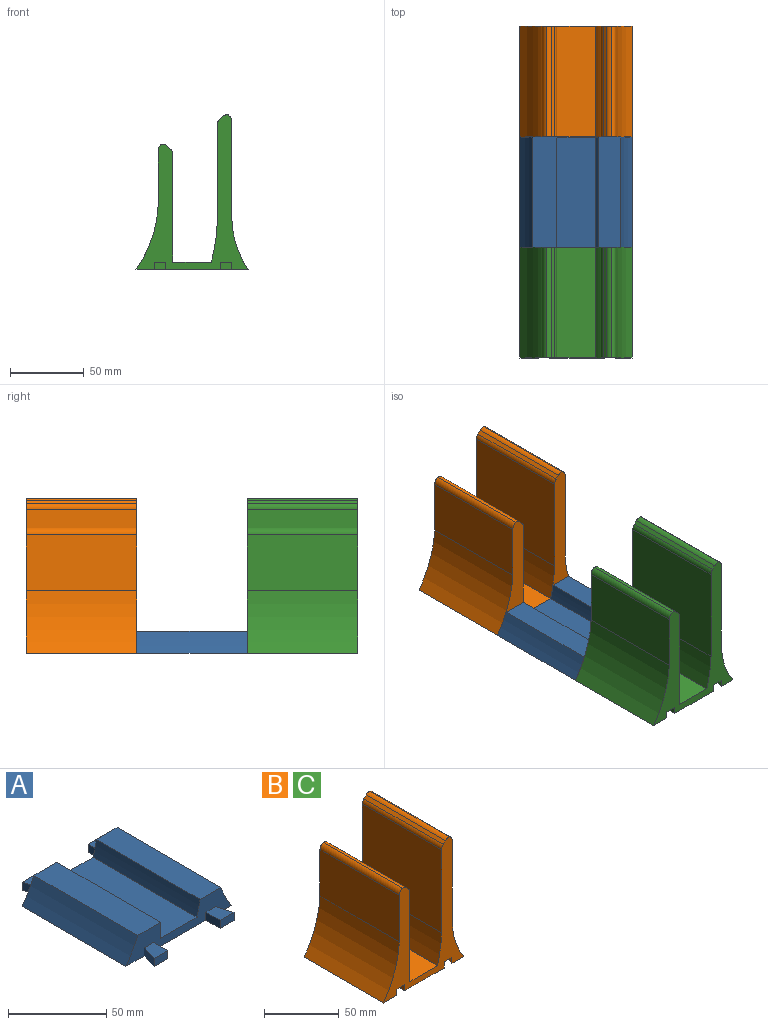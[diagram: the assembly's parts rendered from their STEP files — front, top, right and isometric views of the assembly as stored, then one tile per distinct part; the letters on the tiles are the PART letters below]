
ASSEMBLY  parts=3 mates=1
PART A: 26 faces, bbox 76x95x15 mm
  f0: plane 10.25x10mm, normal (0,0,1), area 86.7mm2, adj f11,f12,f13,f17
  f1: plane 10.25x10mm, normal (0,0,1), area 86.7mm2, adj f11,f14,f15,f16
  f2: plane 74.75x16.48mm, normal (0,0,1), area 1231.5mm2, adj f3,f9,f10,f11
  f3: plane 74.75x10mm, normal (1,0,0), area 747.5mm2, adj f2,f4,f10,f11
  f4: plane 74.75x26.14mm, normal (0,0,1), area 1954.3mm2, adj f3,f5,f10,f11
  f5: cylinder r=117.51mm len=74.75mm, axis (0,-1,0), area 765.7mm2, adj f4,f6,f10,f11
  f6: plane 74.75x15.04mm, normal (0,0,1), area 1124.4mm2, adj f5,f7,f10,f11
  f7: cylinder r=61.84mm len=74.75mm, axis (0,-1,0), area 1261.1mm2, adj f6,f8,f10,f11
  f8: plane 95x76mm, normal (0,0,-1), area 6024.5mm2, adj f7,f9,f10,f11,f12,f13,f14,f15
  f9: cylinder r=80mm len=74.75mm, axis (0,-1,0), area 1292.2mm2, adj f2,f8,f10,f11
  f10: plane 76x15mm, normal (0,1,0), area 664mm2, adj f2,f3,f4,f5,f6,f7,f8,f9
  f11: plane 76x15mm, normal (0,-1,0), area 664.7mm2, adj f0,f1,f2,f3,f4,f5,f6,f7
  f12: plane 10.25x5mm, normal (-1,0,0), area 51.3mm2, adj f0,f8,f11,f13
  f13: plane 10x5mm, normal (0,-1,0), area 50mm2, adj f0,f8,f12,f17
  f14: plane 10.25x5mm, normal (1,0,0), area 51.3mm2, adj f1,f8,f11,f15
  f15: plane 10x5mm, normal (0,-1,0), area 50mm2, adj f1,f8,f14,f16
  f16: plane 10.25x5mm, normal (-0.96,0.29,0), area 53.5mm2, adj f1,f8,f11,f15
  f17: plane 10.25x5mm, normal (0.96,0.29,0), area 53.5mm2, adj f0,f8,f11,f13
  f18: plane 10x5mm, normal (0.96,-0.29,0), area 52.2mm2, adj f8,f10,f20,f21
  f19: plane 10x5mm, normal (-1,0,0), area 50mm2, adj f8,f10,f20,f21
  f20: plane 10x5mm, normal (0,1,0), area 50mm2, adj f8,f18,f19,f21
  f21: plane 10x10mm, normal (0,0,1), area 85mm2, adj f10,f18,f19,f20
  f22: plane 10x5mm, normal (-0.96,-0.29,0), area 52.2mm2, adj f8,f10,f23,f25
  f23: plane 10x5mm, normal (0,1,0), area 50mm2, adj f8,f22,f24,f25
  f24: plane 10x5mm, normal (1,0,0), area 50mm2, adj f8,f10,f23,f25
  f25: plane 10x10mm, normal (0,0,1), area 85mm2, adj f10,f22,f23,f24
PART B: 35 faces, bbox 76x75x105 mm
  f0: plane 105x76mm, normal (0,1,0), area 2322mm2, adj f1,f2,f3,f4,f5,f6,f7,f8
  f1: plane 76x75mm, normal (0,0,-1), area 5329mm2, adj f0,f2,f9,f10,f21,f22,f23,f24
  f2: cylinder r=61.84mm len=75mm, axis (0,1,0), area 2809mm2, adj f0,f1,f3,f10
  f3: plane 75x65.24mm, normal (1,0,0), area 4893.3mm2, adj f0,f2,f10,f17
  f4: plane 75x67.93mm, normal (-1,0,0), area 5094.7mm2, adj f0,f5,f10,f16
  f5: cylinder r=117.51mm len=75mm, axis (0,1,0), area 1900.8mm2, adj f0,f4,f6,f10
  f6: plane 75x26.14mm, normal (0,0,1), area 1960.9mm2, adj f0,f5,f7,f10
  f7: plane 75x72.93mm, normal (1,0,0), area 5469.7mm2, adj f0,f6,f10,f13
  f8: plane 75x37.95mm, normal (-1,0,0), area 2846.2mm2, adj f0,f9,f10,f18
  f9: cylinder r=80mm len=75mm, axis (0,1,0), area 3426.6mm2, adj f0,f1,f8,f10
  f10: plane 105x76mm, normal (0,-1,0), area 2322mm2, adj f1,f2,f3,f4,f5,f6,f7,f8
  f11: plane 75x2.07mm, normal (-0.71,0,0.71), area 219.7mm2, adj f0,f10,f15,f16
  f12: plane 75x2.07mm, normal (0.71,0,0.71), area 219.7mm2, adj f0,f10,f13,f14
  f13: cylinder r=5mm len=75mm, axis (0,-1,0), area 294.5mm2, adj f0,f7,f10,f12
  f14: cylinder r=5mm len=75mm, axis (0,1,0), area 294.5mm2, adj f0,f10,f12,f18
  f15: cylinder r=5mm len=75mm, axis (0,1,0), area 294.5mm2, adj f0,f10,f11,f17
  f16: cylinder r=5mm len=75mm, axis (0,-1,0), area 294.5mm2, adj f0,f4,f10,f11
  f17: cylinder r=5mm len=75mm, axis (0,1,0), area 428.9mm2, adj f0,f3,f10,f15
  f18: cylinder r=5mm len=75mm, axis (0,-1,0), area 428.9mm2, adj f0,f8,f10,f14
  f19: plane 10.59x10.25mm, normal (0,0,-1), area 92.7mm2, adj f0,f24,f25,f26
  f20: plane 10.59x10.25mm, normal (0,0,-1), area 92.7mm2, adj f0,f21,f22,f23
  f21: plane 10.25x5mm, normal (-0.96,-0.29,0), area 53.5mm2, adj f0,f1,f20,f23
  f22: plane 10.25x5mm, normal (1,0,0), area 51.3mm2, adj f0,f1,f20,f23
  f23: plane 10.59x5mm, normal (0,1,0), area 52.9mm2, adj f1,f20,f21,f22
  f24: plane 10.25x5mm, normal (0.96,-0.29,0), area 53.5mm2, adj f0,f1,f19,f26
  f25: plane 10.25x5mm, normal (-1,0,0), area 51.3mm2, adj f0,f1,f19,f26
  f26: plane 10.59x5mm, normal (0,1,0), area 52.9mm2, adj f1,f19,f24,f25
  f27: plane 10.25x5mm, normal (0.96,0.29,0), area 53.5mm2, adj f1,f10,f28,f30
  f28: plane 10.59x5mm, normal (0,-1,0), area 52.9mm2, adj f1,f27,f29,f30
  f29: plane 10.25x5mm, normal (-1,0,0), area 51.2mm2, adj f1,f10,f28,f30
  f30: plane 10.59x10.25mm, normal (0,0,-1), area 92.7mm2, adj f10,f27,f28,f29
  f31: plane 10.25x5mm, normal (-0.96,0.29,0), area 53.5mm2, adj f1,f10,f33,f34
  f32: plane 10.25x5mm, normal (1,0,0), area 51.2mm2, adj f1,f10,f33,f34
  f33: plane 10.59x5mm, normal (0,-1,0), area 52.9mm2, adj f1,f31,f32,f34
  f34: plane 10.59x10.25mm, normal (0,0,-1), area 92.7mm2, adj f10,f31,f32,f33
PART C: same geometry as B
PLACE A t=(-76.3,-138.59,-33.34)mm
PLACE B t=(-76.32,11.53,-33.34)mm
PLACE C t=(-76.32,-138.47,-33.34)mm
MATE fastened A.f21 <-> B.f34  axis (0,0,1) through (-39.5,-58.3,-33.34)mm
